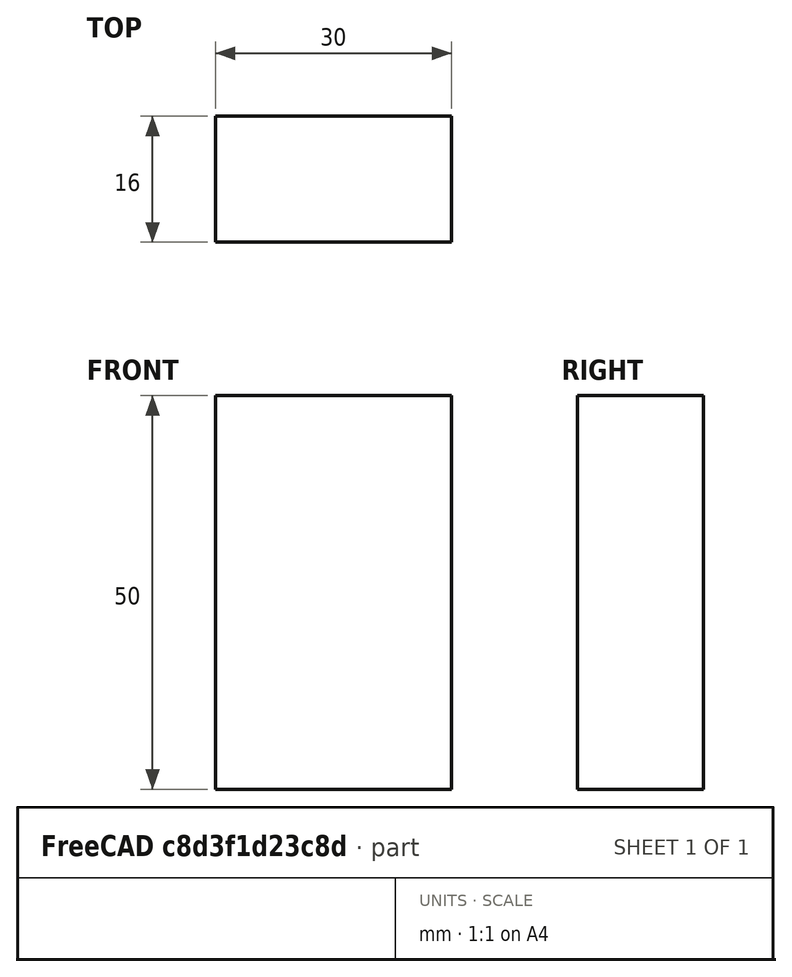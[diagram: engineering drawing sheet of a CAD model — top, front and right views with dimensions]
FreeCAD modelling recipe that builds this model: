
FCSTD DOCUMENT  (FreeCAD 0.15R4671 (Git))
Label: Flat Bar 30x16 EN10058 S235JR
License: All rights reserved
LicenseURL: http://en.wikipedia.org/wiki/All_rights_reserved
objects: Sketcher::SketchObject×1, Part::Extrusion×1
note: 2 computed .brp shape members not serialized (recipe doc carries the construction recipe); baked Part::Feature solids carry a one-line shape summary decoded from their .brp

FEATURE [Sketcher::SketchObject] Sketch
  sketch-geometry (4):
    g0: LineSegment StartX=-15 StartY=-8 StartZ=0 EndX=15 EndY=-8 EndZ=0
    g1: LineSegment StartX=15 StartY=-8 StartZ=0 EndX=15 EndY=8 EndZ=0
    g2: LineSegment StartX=15 StartY=8 StartZ=0 EndX=-15 EndY=8 EndZ=0
    g3: LineSegment StartX=-15 StartY=8 StartZ=0 EndX=-15 EndY=-8 EndZ=0
  constraints (12):
    c: Coincident(g0,g1)
    c: Coincident(g1,g2)
    c: Coincident(g2,g3)
    c: Coincident(g3,g0)
    c: Horizontal(g0)
    c: Horizontal(g2)
    c: Vertical(g1)
    c: Vertical(g3)
    c: Symmetric(g1,g2,g-2)
    c: Symmetric(g0,g1,g-1)
    c: DistanceY(g1) = 16
    c: DistanceX(g0) = 30
FEATURE [Part::Extrusion] Extrude  label="Flat Bar 30x16 EN10058 S235JR"
  Base = -> Sketch
  Dir = (0,0,50)
  Solid = true
